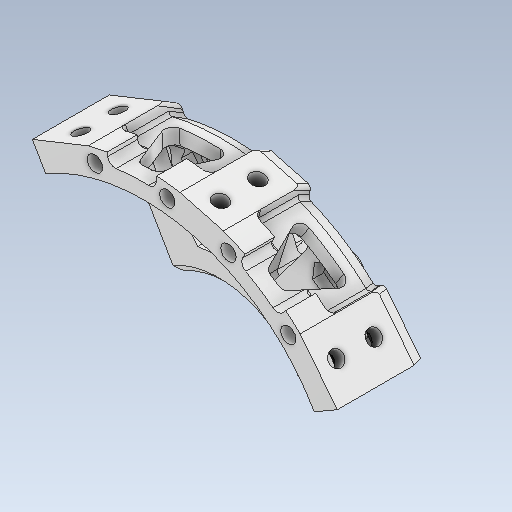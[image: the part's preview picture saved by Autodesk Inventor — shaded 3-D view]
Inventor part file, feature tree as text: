
AUTODESK INVENTOR PART (.ipt)
format: ipt  version: 2020 (Build 240168000, 168)  size: 1,173,504 bytes
history: native  units: mm
features: sketch x21, projected_geometry x20, extrude x18, fillet x13, mirror x7, chamfer x7, plane x4, other x4, revolve x3, thicken_offset x3, reference x1
ambient origin geometry x8: Origin, YZ Plane, XZ Plane, XY Plane, X Axis, Y Axis, Z Axis, Center Point
bodies: Solid1 (feature_tree)
feature tree (101):
  extrude  "Extrusion1"  Depth=105.0mm
  extrude  "Extrusion2"  TaperAngle=90.0deg  [1 undecoded]
  extrude  "Extrusion3"  Depth=20.0mm
  revolve  "Revolution1"  Angle=45.0deg
  revolve  "Revolution2"  [1 undecoded]
  extrude  "Extrusion4"  Depth=6.0mm
  plane  "Work Plane1"
  extrude  "Extrusion5"  Depth=0.872665mm
  mirror  "Mirror1"
  extrude  "Extrusion7"  Depth=8.0mm
  extrude  "Extrusion8"  Depth=4.0mm TaperAngle=0.0deg
  plane  "Work Plane2"
  extrude  "Extrusion9"  Depth=3.5mm
  mirror  "Mirror2"
  extrude  "Extrusion10"  Depth=10.0mm TaperAngle=0.0deg
  extrude  "Extrusion11"  Depth=7.0mm
  plane  "Work Plane3"
  extrude  "Extrusion12"  Depth=10.0mm
  extrude  "Extrusion13"  Depth=10.0mm
  mirror  "Mirror3"
  extrude  "Extrusion14"  Depth=10.0mm
  mirror  "Mirror4"
  fillet  "Fillet1"  Radius=10.0mm
  fillet  "Fillet2"  [1 undecoded]
  revolve  "Revolution3"  Angle=360.0deg
  extrude  "Extrusion15"  Depth=60.0mm TaperAngle=360.0deg
  extrude  "Extrusion16"  Depth=7.0mm
  extrude  "Extrusion17"  Depth=6.0mm
  mirror  "Mirror5"
  extrude  "Extrusion18"  Depth=10.0mm
  fillet  "Fillet3"  Radius=4.0mm
  fillet  "Fillet4"  Radius=10.0mm
  mirror  "Mirror6"
  plane  "Work Plane4"
  extrude  "Extrusion19"  Depth=10.0mm TaperAngle=0.0deg
  fillet  "Fillet5"  [1 undecoded]
  fillet  "Fillet6"  Radius=4.2mm
  mirror  "Mirror7"
  thicken_offset  "Thicken1"
  thicken_offset  "Thicken2"
  chamfer  "Chamfer1"  Distance=60.0mm Angle=360.0deg
  chamfer  "Chamfer3"  Distance=4.2mm
  thicken_offset  "Thicken3"
  chamfer  "Chamfer5"  Distance=60.0mm Angle=360.0deg
  fillet  "Fillet7"  Radius=3.5mm
  fillet  "Fillet8"  Radius=0.872665mm
  chamfer  "Chamfer6"  Distance=1.047198mm
  chamfer  "Chamfer7"  Distance=8.0mm
  fillet  "Fillet9"  Radius=1.0mm
  fillet  "Fillet10"  Radius=3.5mm
  chamfer  "Chamfer8"  Distance=4.1mm
  fillet  "Fillet12"  Radius=3.0mm
  fillet  "Fillet13"  Radius=3.5mm
  fillet  "Fillet14"  Radius=4.1mm
  chamfer  "Chamfer9"  Distance=5.0mm
  sketch  "Sketch1"  dims[d0=113.0mm d1=105.0mm]
  reference  "Reference1"
  sketch  "Sketch2"  dims[d2=30.0deg d3=90.0deg]
  sketch  "Sketch3"  dims[d4=20.0mm d5=0.0mm d6=45.0mm]
  projected_geometry  "Projected Loop1"
  projected_geometry  "Projected Loop2"
  sketch  "Sketch4"  dims[d7=53.0mm d8=45.0deg]
  projected_geometry  "Projected Loop3"
  sketch  "Sketch5"  dims[d9=45.0deg d10=18.0mm d11=0.0mm]
  projected_geometry  "Projected Loop4"
  sketch  "Sketch6"  dims[d12=4.0mm d13=0.0mm d14=6.0mm]
  projected_geometry  "Projected Loop5"
  sketch  "Sketch7"  dims[d15=0.872665mm d16=0.872665mm]
  projected_geometry  "Projected Loop6"
  sketch  "Sketch8"  dims[d17=7.0mm d18=8.0mm]
  projected_geometry  "Projected Loop7"
  projected_geometry  "Projected Loop8"
  sketch  "Sketch9"  dims[d19=7.0mm d20=4.0mm d21=0.0mm]
  projected_geometry  "Projected Loop9"
  sketch  "Sketch10"  dims[d22=4.0mm d23=3.5mm]
  sketch  "Sketch11"  dims[d24=4.2mm d25=10.0mm d26=0.0mm]
  projected_geometry  "Projected Loop10"
  sketch  "Sketch12"  dims[d27=15.0mm d28=7.0mm]
  projected_geometry  "Projected Loop11"
  sketch  "Sketch13"  dims[d31=10.0mm d32=0.0mm d33=7.5mm]
  projected_geometry  "Projected Loop12"
  sketch  "Sketch14"  dims[d34=5.0mm d35=10.0mm]
  projected_geometry  "Projected Loop13"
  sketch  "Sketch15"  dims[d36=4.0mm d37=4.0mm d38=10.0mm d39=0.0mm d40=-7.0mm]
  sketch  "Sketch17"  dims[d47=4.2mm d48=60.0mm d50=360.0deg]
  projected_geometry  "Projected Loop15"
  projected_geometry  "Projected Loop16"
  sketch  "Sketch18"  dims[d52=4.2mm d53=60.0mm d55=360.0deg]
  projected_geometry  "Projected Loop17"
  sketch  "Sketch19"  dims[d57=3.5mm d58=0.0mm d59=7.0mm]
  projected_geometry  "Projected Loop18"
  sketch  "Sketch20"  dims[d60=6.0mm d61=6.0mm]
  projected_geometry  "Projected Loop19"
  sketch  "Sketch21"  dims[d62=2.0mm d63=0.0mm d64=5.0mm d65=4.0mm d66=10.0mm]
  projected_geometry  "Projected Loop20"
  sketch  "Sketch22"  dims[d67=4.0mm d68=10.0mm d69=0.0mm d70=-8.0mm d71=4.2mm d72=60.0mm d74=360.0deg d76=4.2mm d77=60.0mm d79=360.0deg d81=3.5mm d82=0.0mm d83=0.872665mm d84=1.047198mm d85=8.0mm d86=0.0mm d87=1.0mm d88=3.5mm d89=4.1mm d90=3.0mm d91=3.5mm d92=4.1mm d93=5.0mm d94=0.0mm d95=2.0mm d96=2.0mm d97=10.0mm d98=20.0mm d99=30.0mm d100=0.872665mm d101=48.0mm d102=3.839724mm d103=4.0mm d104=15.0mm d105=4.0mm d106=10.0mm d107=0.0mm d108=4.2mm d109=60.0mm d111=360.0deg d113=4.2mm d114=60.0mm d116=360.0deg d118=3.0mm d119=0.0mm d120=10.0mm d121=10.0mm d122=2.5mm d123=0.0mm d124=2.0mm d125=7.0mm d126=7.0mm d127=2.0mm d128=5.0mm d129=0.0mm d130=2.0mm d131=2.0mm d132=1.0mm d133=1.5mm d134=9.0mm d135=10.8mm d136=9.0mm d137=9.0mm d138=15.0mm d139=2.5mm d140=2.5mm d143=15.0mm d144=0.0mm d145=2.0mm d146=2.0mm d147=1.0mm d148=1.0mm d149=1.0mm d150=1.0mm d151=1.5mm d152=2.5mm d153=30.0deg d157=1.5mm d158=2.5mm d159=30.0deg d163=0.5mm d164=0.5mm d165=2.0mm d166=2.5mm d167=60.0deg d168=8.0mm d169=8.0mm d170=1.5mm d171=2.5mm d172=60.0deg d173=1.5mm d174=2.5mm d175=60.0deg d176=3.0mm d177=1.5mm d179=2.0mm d180=2.5mm d181=60.0deg d182=1.0mm d183=1.0mm d184=2.0mm d186=2.0mm d187=2.5mm d188=60.0deg]
  projected_geometry  "Projected Loop21"
  parser-record x1  (decoder bookkeeping rows leaked as tree rows — omitted from the tree; the rows remain in map.json)
  other  "reducer_2.iam"
  other  "xl_wheel_ass:1"
  other  "xl_60_ori:1"
note: 4 required parameter values undecoded (feature->parameter linkage not recoverable at this tier; creation-order binding heuristic only, values carry confidence <= 0.55)
note: 1 file-system path scrubbed to <path> (originals preserved in map.json)